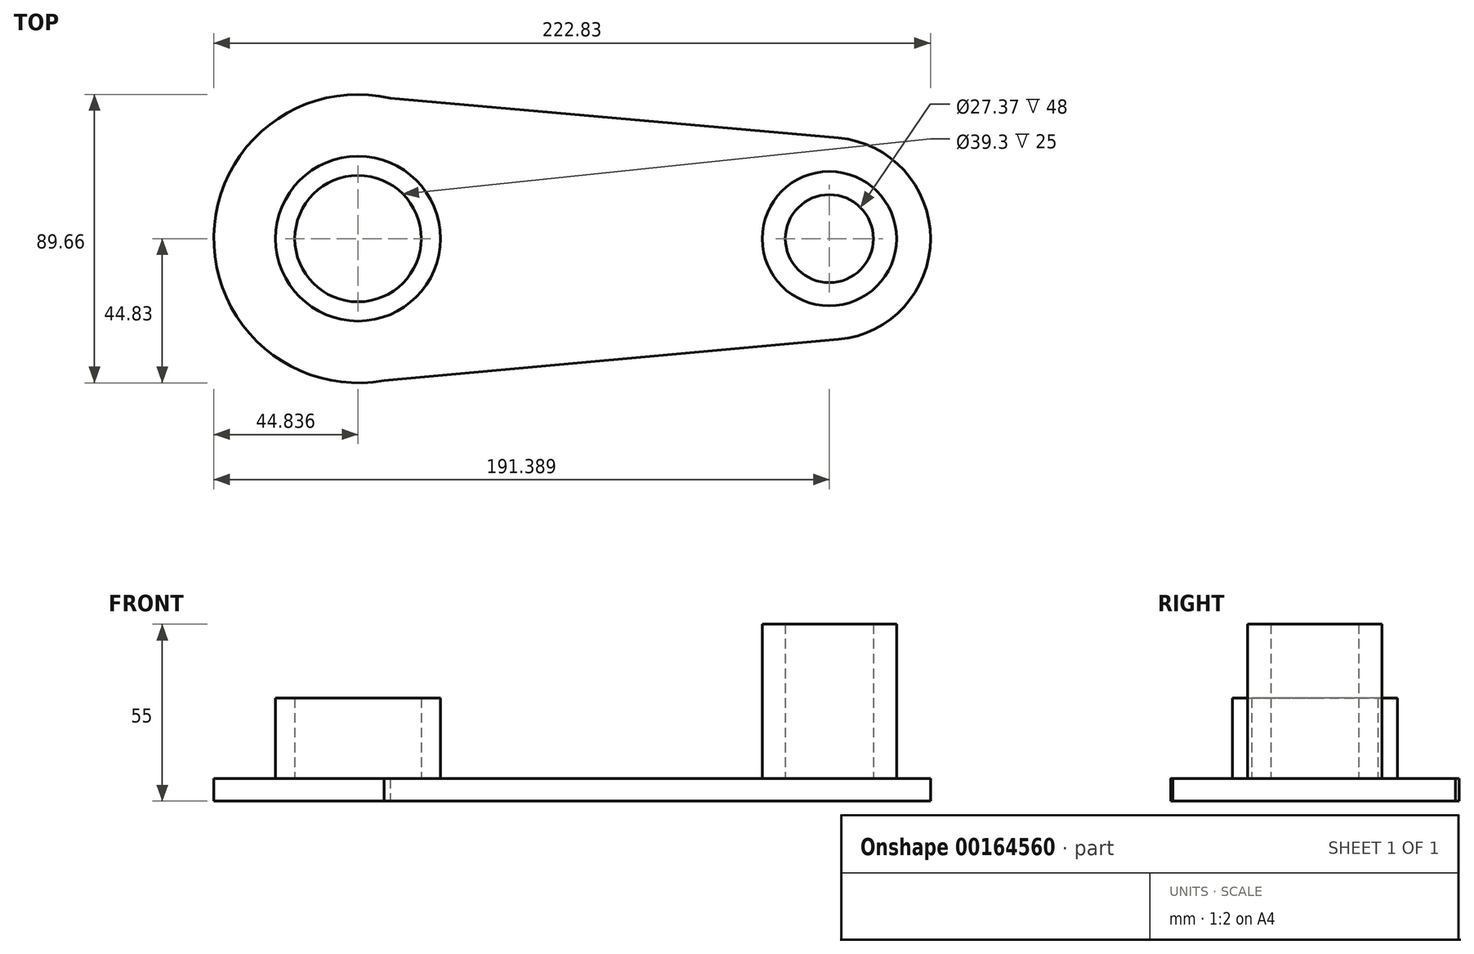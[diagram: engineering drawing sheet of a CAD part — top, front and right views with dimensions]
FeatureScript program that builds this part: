
annotation { "Feature Type Name" : "Feature", "Feature Type Description" : "" }
export const myFeature = defineFeature(function(context is Context, id is Id, definition is map)
    precondition{}
    {
        {
            var Q0;
            Q0=qCreatedBy(makeId("Top.planeOp"),FACE);
            var sketch = newSketch(context, id + "F0", { "sketchPlane" : qUnion([Q0])});
            skCircle(sketch, "E0", {"center": v(-88.93, 0) * mm, "radius": 44.83 * mm});
            skCircle(sketch, "E1", {"center": v(57.62, 0) * mm, "radius": 31.44 * mm});
            skLineSegment(sketch, "E2", {"start": v(-91.02, 44.79) * mm, "end": v(60.4, 31.32) * mm});
            skLineSegment(sketch, "E3", {"start": v(-88.94, -44.83) * mm, "end": v(60.45, -31.32) * mm});
            skSolve(sketch);
        }
        {
            var Q0;
            Q0 = qSketchRegion(id + "F0", true);
            extrude(context, id + "F1", {"entities" : qUnion([Q0]), "depth" : 7 * mm});
        }
        {
            var Q0;
            Q0=makeQuery(id+"F1.opExtrude","CAP_FACE",FACE,{"disambiguationData":[OSD([sQuery(id+"F0.wireOp",EDGE,"E0"),sQuery(id+"F0.wireOp",EDGE,"E1"),sQuery(id+"F0.wireOp",EDGE,"E2"),sQuery(id+"F0.wireOp",EDGE,"E3")])],"isStart":false});
            var sketch = newSketch(context, id + "F2", { "sketchPlane" : qUnion([Q0])});
            skCircle(sketch, "E4", {"center": v(57.62, 0) * mm, "radius": 20.88 * mm});
            skCircle(sketch, "E5", {"center": v(57.62, 0) * mm, "radius": 13.68 * mm});
            skSolve(sketch);
        }
        {
            var Q0;
            Q0 = qSketchRegion(id + "F2", true);
            extrude(context, id + "F3", {"entities" : qUnion([Q0]), "operationType" : NewBodyOperationType.ADD, "depth" : 48 * mm});
        }
        {
            var Q0;
            {var subQ0=sQuery(id+"F0.wireOp",EDGE,"E3");var subQ1=sQuery(id+"F0.wireOp",EDGE,"E2");var subQ2=sQuery(id+"F0.wireOp",EDGE,"E1");var subQ3=sQuery(id+"F0.wireOp",EDGE,"E0");Q0=makeQuery(id+"F3.boolean.opBoolean","SPLIT",FACE,{"disambiguationData":[TD([makeQuery(id+"F1.opExtrude","SWEPT_FACE",FACE,{"disambiguationData":[OSD([subQ3])]})])],"derivedFrom":makeQuery(id+"F1.opExtrude","CAP_FACE",FACE,{"disambiguationData":[OSD([subQ3,subQ2,subQ1,subQ0])],"isStart":false})});}
            var sketch = newSketch(context, id + "F4", { "sketchPlane" : qUnion([Q0])});
            skCircle(sketch, "E6", {"center": v(-88.93, 0) * mm, "radius": 25.63 * mm});
            skCircle(sketch, "E7", {"center": v(-88.93, 0) * mm, "radius": 19.65 * mm});
            skSolve(sketch);
        }
        {
            var Q0;
            Q0 = qSketchRegion(id + "F4", true);
            extrude(context, id + "F5", {"entities" : qUnion([Q0]), "operationType" : NewBodyOperationType.ADD, "depth" : 25 * mm});
        }
    });
